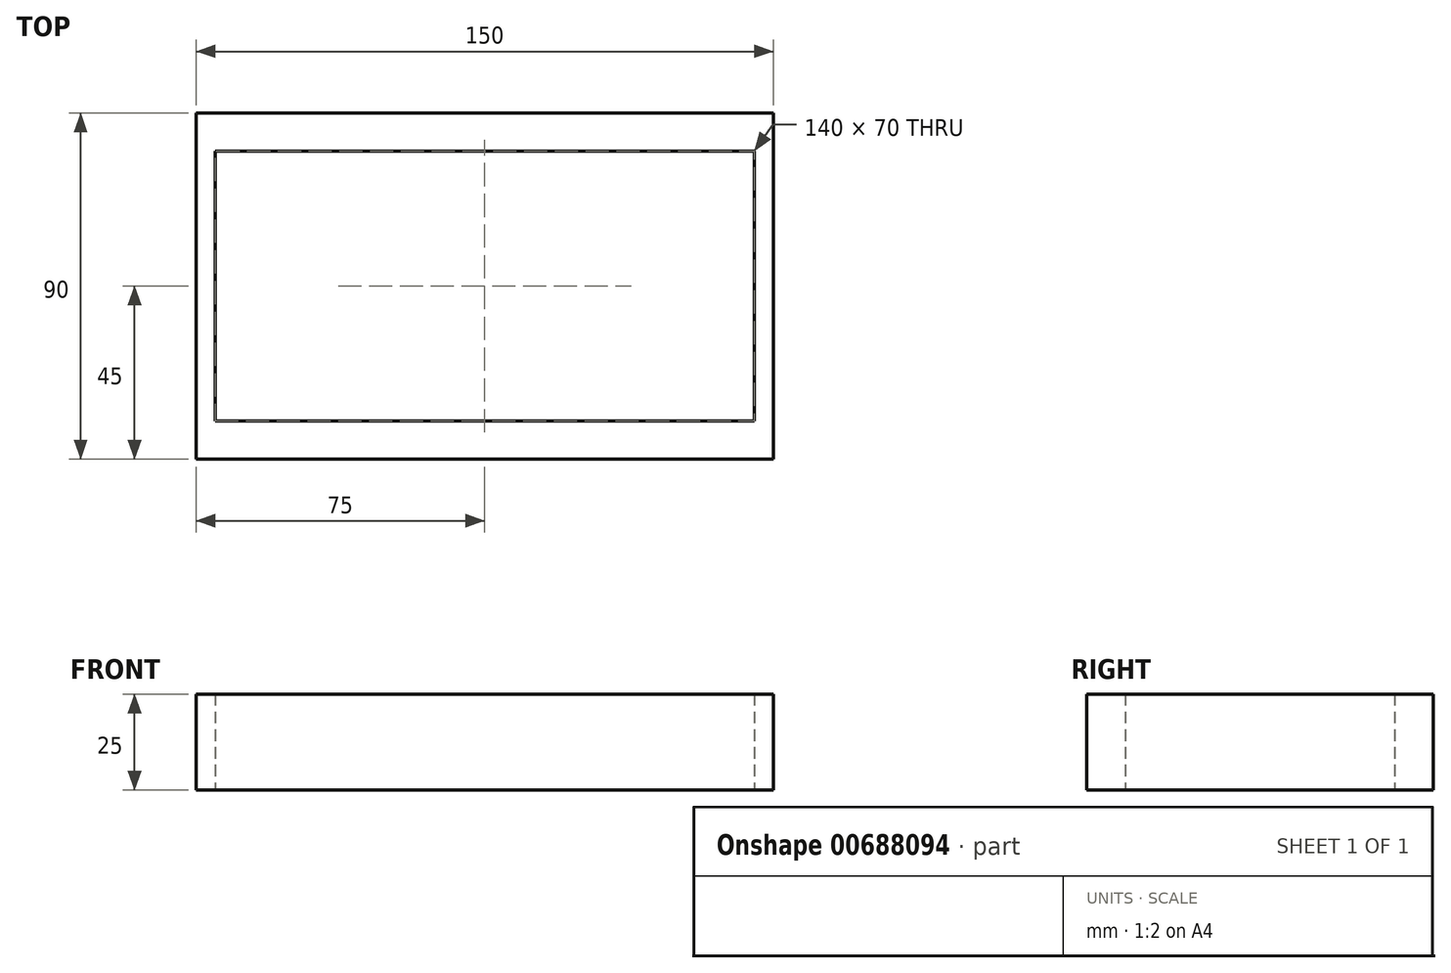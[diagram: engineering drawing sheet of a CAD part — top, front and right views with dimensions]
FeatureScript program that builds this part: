
annotation { "Feature Type Name" : "Feature", "Feature Type Description" : "" }
export const myFeature = defineFeature(function(context is Context, id is Id, definition is map)
    precondition{}
    {
        {
            var Q0;
            Q0=qCreatedBy(makeId("Top.planeOp"),FACE);
            var sketch = newSketch(context, id + "F0", { "sketchPlane" : qUnion([Q0])});
            skLineSegment(sketch, "E0.bottom", {"start": v(0, 0) * mm, "end": v(150, 0) * mm});
            skLineSegment(sketch, "E0.top", {"start": v(0, -90) * mm, "end": v(150, -90) * mm});
            skLineSegment(sketch, "E0.left", {"start": v(0, 0) * mm, "end": v(0, -90) * mm});
            skLineSegment(sketch, "E0.right", {"start": v(150, 0) * mm, "end": v(150, -90) * mm});
            skLineSegment(sketch, "E1.bottom", {"start": v(5, -10) * mm, "end": v(145, -10) * mm});
            skLineSegment(sketch, "E1.top", {"start": v(5, -80) * mm, "end": v(145, -80) * mm});
            skLineSegment(sketch, "E1.left", {"start": v(5, -10) * mm, "end": v(5, -80) * mm});
            skLineSegment(sketch, "E1.right", {"start": v(145, -10) * mm, "end": v(145, -80) * mm});
            skLineSegment(sketch, "E2.bottom", {"start": v(60.32, -80) * mm, "end": v(55.32, -80) * mm});
            skLineSegment(sketch, "E2.top", {"start": v(60.32, -55) * mm, "end": v(55.32, -55) * mm});
            skLineSegment(sketch, "E2.left", {"start": v(60.32, -80) * mm, "end": v(60.32, -55) * mm});
            skLineSegment(sketch, "E2.right", {"start": v(55.32, -80) * mm, "end": v(55.32, -55) * mm});
            skLineSegment(sketch, "E3.bottom", {"start": v(55.32, -10) * mm, "end": v(60.32, -10) * mm});
            skLineSegment(sketch, "E3.top", {"start": v(55.32, -35) * mm, "end": v(60.32, -35) * mm});
            skLineSegment(sketch, "E3.left", {"start": v(55.32, -10) * mm, "end": v(55.32, -35) * mm});
            skLineSegment(sketch, "E3.right", {"start": v(60.32, -10) * mm, "end": v(60.32, -35) * mm});
            skSolve(sketch);
        }
        {
            var Q0;
            Q0 = qSketchRegion(id + "F0", true);
            var Q1;
            Q1=makeQuery(id+"F0.imprint","IMPRINT",FACE,{"disambiguationData":[TD([[makeQuery(id+"F0.imprint","IMPRINT",EDGE,{"derivedFrom":sQuery(id+"F0.wireOp",EDGE,"E3.bottom")}),-1.0]])]});
            var Q2;
            Q2=makeQuery(id+"F0.imprint","IMPRINT",FACE,{"disambiguationData":[TD([[makeQuery(id+"F0.imprint","IMPRINT",EDGE,{"derivedFrom":sQuery(id+"F0.wireOp",EDGE,"E2.bottom")}),-1.0]])]});
            extrude(context, id + "F1", {"entities" : qUnion([Q0, Q1, Q2]), "depth" : 25 * mm, "offsetDistance" : 25 * mm});
        }
    });
